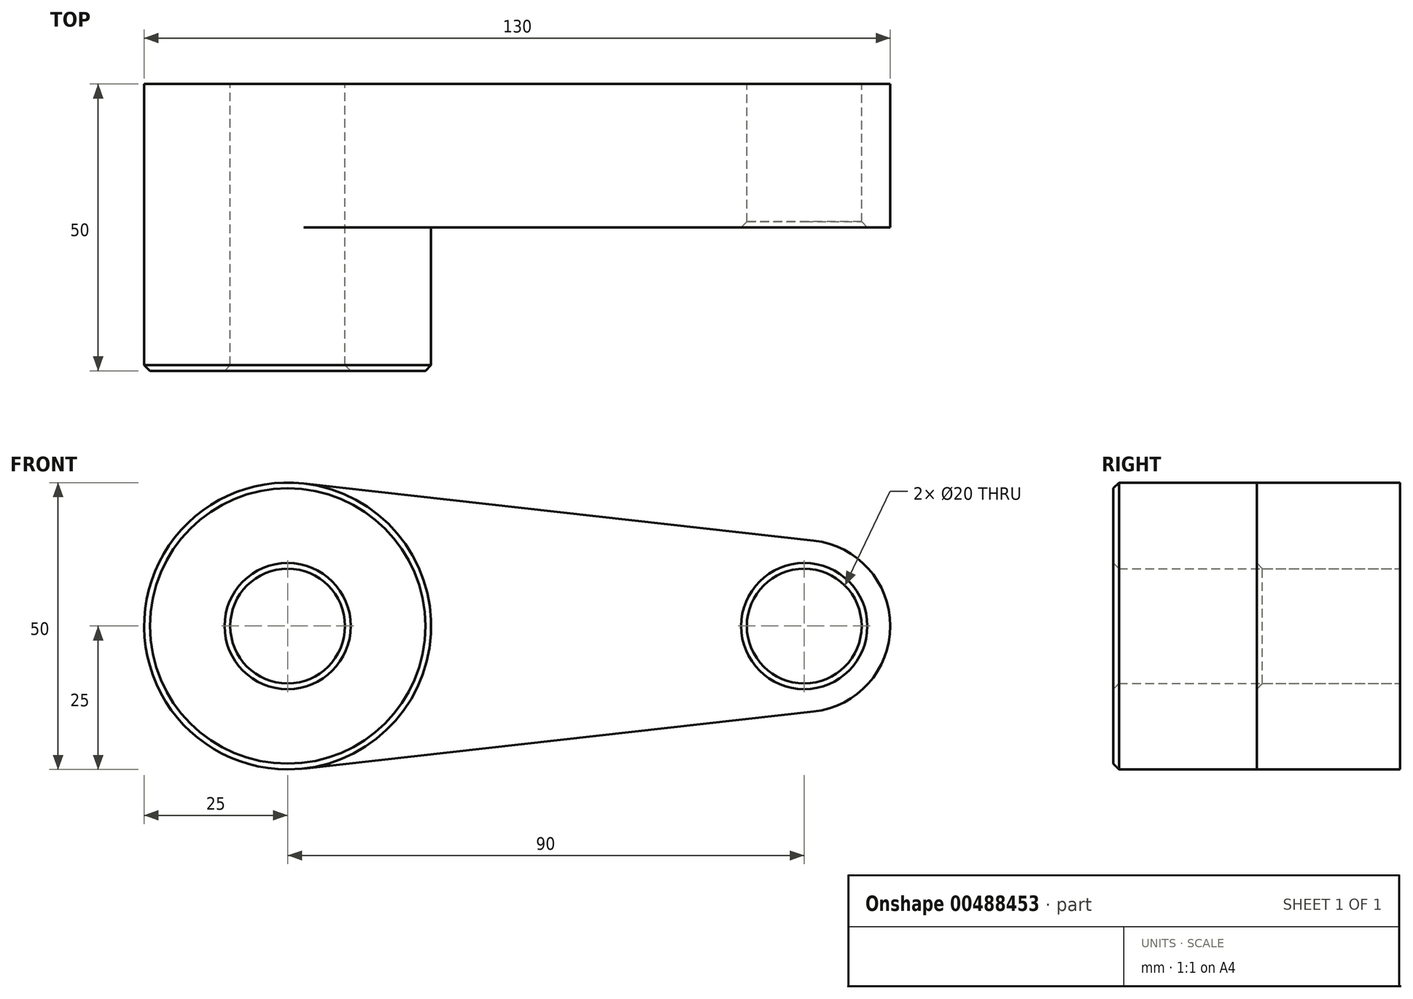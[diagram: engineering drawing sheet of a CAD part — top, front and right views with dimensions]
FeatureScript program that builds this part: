
annotation { "Feature Type Name" : "Feature", "Feature Type Description" : "" }
export const myFeature = defineFeature(function(context is Context, id is Id, definition is map)
    precondition{}
    {
        {
            var Q0;
            Q0=qCreatedBy(makeId("Front.planeOp"),FACE);
            var sketch = newSketch(context, id + "F0", { "sketchPlane" : qUnion([Q0])});
            skCircle(sketch, "E0", {"center": v(0, 0) * mm, "radius": 25 * mm});
            skCircle(sketch, "E1", {"center": v(90, 0) * mm, "radius": 15 * mm});
            skLineSegment(sketch, "E2", {"start": v(2.78, 24.85) * mm, "end": v(91.67, 14.9) * mm});
            skLineSegment(sketch, "E3", {"start": v(2.78, -24.85) * mm, "end": v(91.67, -14.9) * mm});
            skCircle(sketch, "E4", {"center": v(0, 0) * mm, "radius": 10 * mm});
            skCircle(sketch, "E5", {"center": v(90, 0) * mm, "radius": 10 * mm});
            skSolve(sketch);
        }
        {
            var Q0;
            Q0 = qSketchRegion(id + "F0", true);
            extrude(context, id + "F1", {"entities" : qUnion([Q0]), "depth" : 25 * mm});
        }
        {
            var Q0;
            Q0=makeQuery(id+"F0.imprint","IMPRINT",FACE,{"disambiguationData":[TD([[makeQuery(id+"F0.imprint","IMPRINT",EDGE,{"derivedFrom":sQuery(id+"F0.wireOp",EDGE,"E4")}),-1.0]])]});
            extrude(context, id + "F2", {"entities" : qUnion([Q0]), "operationType" : NewBodyOperationType.ADD, "depth" : 50 * mm});
        }
        {
            var Q0;
            Q0=makeQuery(id+"F2.opExtrude","CAP_EDGE",EDGE,{"disambiguationData":[OSD([sQuery(id+"F0.wireOp",EDGE,"E0")])],"isStart":false});
            chamfer(context, id + "F3", {"entities" : qUnion([Q0]), "width" : 1 * mm, "tangentPropagation" : true});
        }
        {
            var Q0;
            Q0=makeQuery(id+"F1.opExtrude","CAP_EDGE",EDGE,{"disambiguationData":[OSD([sQuery(id+"F0.wireOp",EDGE,"E5")])],"isStart":false});
            var Q1;
            Q1=makeQuery(id+"F2.opExtrude","CAP_EDGE",EDGE,{"disambiguationData":[OSD([sQuery(id+"F0.wireOp",EDGE,"E4")])],"isStart":false});
            chamfer(context, id + "F4", {"entities" : qUnion([Q0, Q1]), "width" : 1 * mm, "tangentPropagation" : true});
        }
    });
